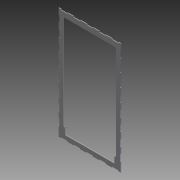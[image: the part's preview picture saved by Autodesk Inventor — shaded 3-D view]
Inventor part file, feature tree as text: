
AUTODESK INVENTOR PART (.ipt)
format: ipt  version: 2011 (Build 150239000, 239)  size: 547,840 bytes
history: native  units: in
note: dims shown in document units (in); Inventor stores cm internally (conversion verified against a paired STEP export)
features: extrude x12, sketch x12, fillet x1
ambient origin geometry x8: Origin, YZ Plane, XZ Plane, XY Plane, X Axis, Y Axis, Z Axis, Center Point
bodies: Solid1 (feature_tree)
feature tree (25):
  extrude  "Extrusion1"  Depth=35.0in
  extrude  "Extrusion2"  Depth=1.5in
  extrude  "Extrusion3"  Depth=0.75in
  extrude  "Extrusion4"  Depth=2.25in
  fillet  "Fillet1"  Radius=0.156in
  extrude  "Extrusion5"  Depth=0.25in TaperAngle=0.0deg
  extrude  "Extrusion6"  Depth=3.0in
  extrude  "Extrusion7"  Depth=1.0in
  extrude  "Extrusion8"  Depth=0.25in TaperAngle=0.0deg
  extrude  "Extrusion9"  Depth=3.5in
  extrude  "Extrusion10"  Depth=3.5in
  extrude  "Extrusion11"  Depth=0.25in TaperAngle=0.0deg
  extrude  "Extrusion12"  Depth=0.25in
  sketch  "Sketch1"  dims[d0=19.5in d1=35.0in]
  sketch  "Sketch2"  dims[d2=0.25in d3=0.0in d4=1.5in]
  sketch  "Sketch3"  dims[d5=3.0in d6=0.75in]
  sketch  "Sketch4"  dims[d7=0.75in d8=2.25in d9=0.156in]
  sketch  "Sketch5"  dims[d10=0.156in d11=0.25in d12=0.0in]
  sketch  "Sketch6"  dims[d13=1.5in d14=3.0in]
  sketch  "Sketch7"  dims[d15=1.5in d16=1.0in]
  sketch  "Sketch8"  dims[d17=32.25in d18=0.25in d19=0.0in]
  sketch  "Sketch9"  dims[d20=2.0in d21=3.5in]
  sketch  "Sketch10"  dims[d22=2.0in d23=3.5in]
  sketch  "Sketch11"  dims[d24=1.5in d25=0.25in d26=0.0in]
  sketch  "Sketch12"  dims[d27=0.25in d28=0.25in d29=0.25in d30=1.0in d31=1.0in d32=1.0in d33=1.0in d34=1.0in d35=1.0in d36=1.0in d37=1.0in d38=1.0in d39=1.0in d40=1.0in d41=1.0in d42=1.0in d43=1.0in d44=1.0in d45=1.0in d46=1.0in d47=1.0in d48=1.0in d49=0.25in d50=0.0in d51=2.0in d52=2.0in d53=2.0in d54=2.0in d55=2.0in d56=2.0in d57=2.0in d58=2.0in d59=2.0in d60=2.0in d61=2.0in d62=2.0in d63=2.0in d64=2.0in d65=2.0in d66=2.0in d67=2.0in d68=0.25in d69=0.0in d70=0.25in d71=0.0in d72=0.25in d73=0.0in d74=0.75in d75=0.25in d76=0.75in d77=0.25in d78=2.0in d79=2.0in d80=2.0in d81=2.0in d82=2.0in d83=2.0in d84=2.0in d85=2.0in d86=0.25in d87=0.0in d88=2.0in d89=2.0in d90=2.0in d91=2.0in d92=0.25in d93=0.0in d94=2.0in d95=2.0in d96=0.25in d97=0.0in d98=0.25in d99=0.25in d100=0.0in]
